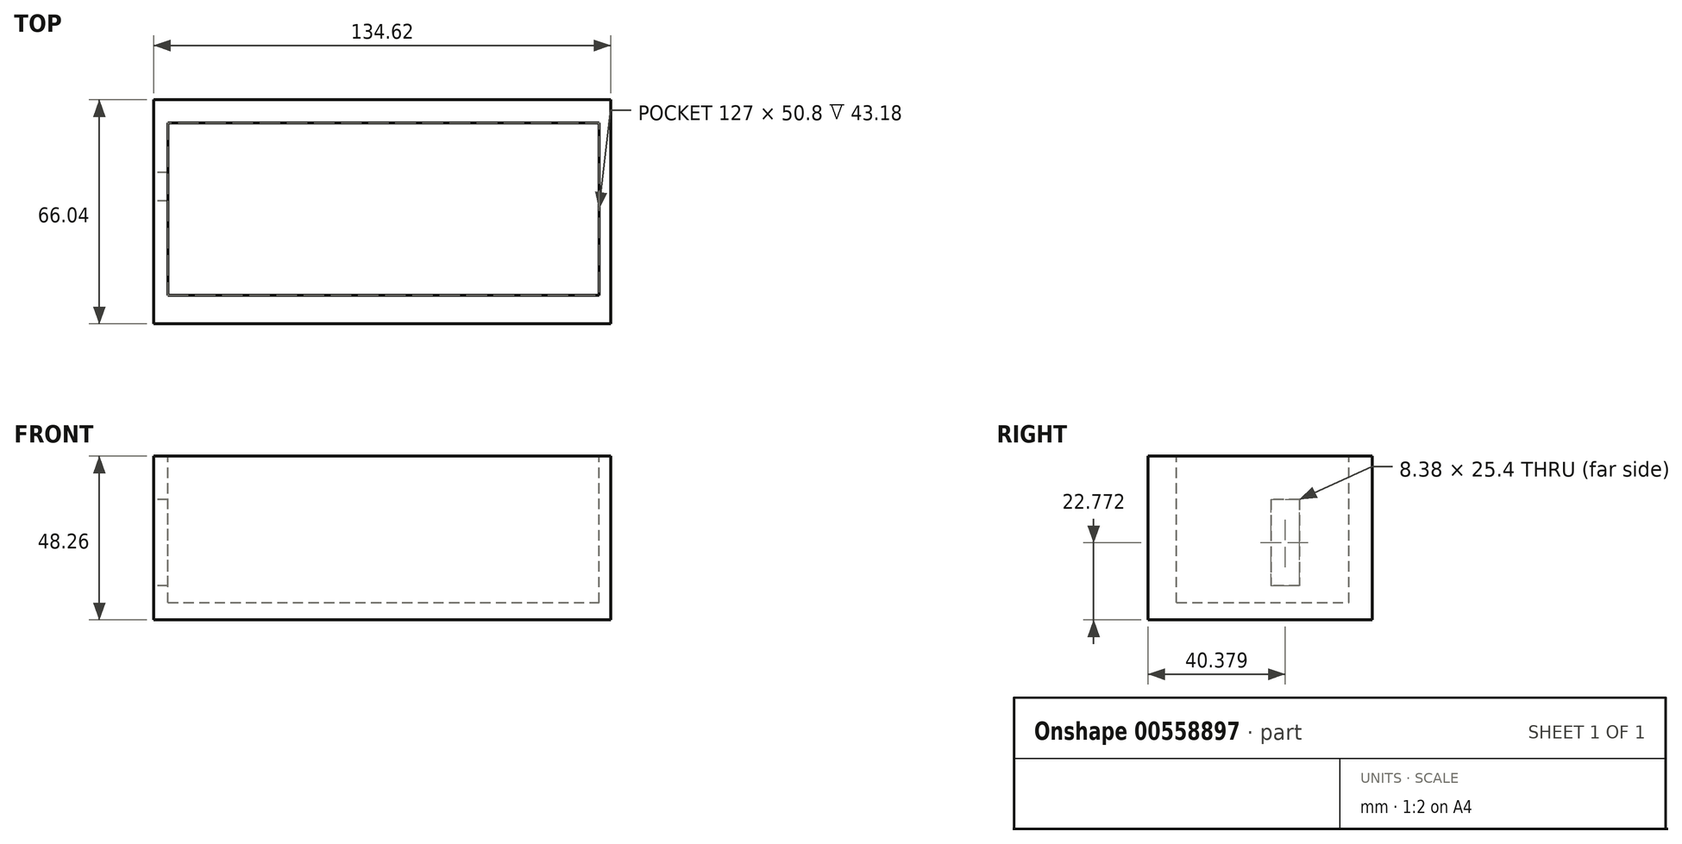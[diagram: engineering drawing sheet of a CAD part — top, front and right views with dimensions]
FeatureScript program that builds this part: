
annotation { "Feature Type Name" : "Feature", "Feature Type Description" : "" }
export const myFeature = defineFeature(function(context is Context, id is Id, definition is map)
    precondition{}
    {
        {
            var Q0;
            Q0=qCreatedBy(makeId("Top.planeOp"),FACE);
            var sketch = newSketch(context, id + "F0", { "sketchPlane" : qUnion([Q0])});
            skLineSegment(sketch, "E0.bottom", {"start": v(-63.14, -44.57) * mm, "end": v(71.48, -44.57) * mm});
            skLineSegment(sketch, "E0.top", {"start": v(-63.14, 21.47) * mm, "end": v(71.48, 21.47) * mm});
            skLineSegment(sketch, "E0.left", {"start": v(-63.14, -44.57) * mm, "end": v(-63.14, 21.47) * mm});
            skLineSegment(sketch, "E0.right", {"start": v(71.48, -44.57) * mm, "end": v(71.48, 21.47) * mm});
            skSolve(sketch);
        }
        {
            var Q0;
            Q0=makeQuery(id+"F0.imprint","IMPRINT",FACE,{"disambiguationData":[TD([[makeQuery(id+"F0.imprint","IMPRINT",EDGE,{"derivedFrom":sQuery(id+"F0.wireOp",EDGE,"E0.bottom")}),1.0]])]});
            extrude(context, id + "F1", {"entities" : qUnion([Q0]), "depth" : 48.26 * mm, "offsetDistance" : 25.4 * mm});
        }
        {
            var Q0;
            Q0=makeQuery(id+"F1.opExtrude","CAP_FACE",FACE,{"disambiguationData":[OSD([sQuery(id+"F0.wireOp",EDGE,"E0.bottom"),sQuery(id+"F0.wireOp",EDGE,"E0.top"),sQuery(id+"F0.wireOp",EDGE,"E0.left"),sQuery(id+"F0.wireOp",EDGE,"E0.right")])],"isStart":false});
            var sketch = newSketch(context, id + "F2", { "sketchPlane" : qUnion([Q0])});
            skLineSegment(sketch, "E1.bottom", {"start": v(-58.95, -36.15) * mm, "end": v(68.05, -36.15) * mm});
            skLineSegment(sketch, "E1.top", {"start": v(-58.95, 14.65) * mm, "end": v(68.05, 14.65) * mm});
            skLineSegment(sketch, "E1.left", {"start": v(-58.95, -36.15) * mm, "end": v(-58.95, 14.65) * mm});
            skLineSegment(sketch, "E1.right", {"start": v(68.05, -36.15) * mm, "end": v(68.05, 14.65) * mm});
            skSolve(sketch);
        }
        {
            var Q0;
            Q0=makeQuery(id+"F2.imprint","IMPRINT",FACE,{"disambiguationData":[TD([[makeQuery(id+"F2.imprint","IMPRINT",EDGE,{"derivedFrom":sQuery(id+"F2.wireOp",EDGE,"E1.bottom")}),1.0]])]});
            extrude(context, id + "F3", {"entities" : qUnion([Q0]), "operationType" : NewBodyOperationType.REMOVE, "oppositeDirection" : true, "depth" : 43.18 * mm, "offsetDistance" : 25.4 * mm});
        }
        {
            var Q0;
            Q0=makeQuery(id+"F1.opExtrude","SWEPT_FACE",FACE,{"disambiguationData":[OSD([sQuery(id+"F0.wireOp",EDGE,"E0.left")])]});
            var sketch = newSketch(context, id + "F4", { "sketchPlane" : qUnion([Q0])});
            skLineSegment(sketch, "E2.bottom", {"start": v(0, 35.47) * mm, "end": v(8.38, 35.47) * mm});
            skLineSegment(sketch, "E2.top", {"start": v(0, 10.07) * mm, "end": v(8.38, 10.07) * mm});
            skLineSegment(sketch, "E2.left", {"start": v(0, 35.47) * mm, "end": v(0, 10.07) * mm});
            skLineSegment(sketch, "E2.right", {"start": v(8.38, 35.47) * mm, "end": v(8.38, 10.07) * mm});
            skSolve(sketch);
        }
        {
            var Q0;
            Q0=makeQuery(id+"F4.imprint","IMPRINT",FACE,{"disambiguationData":[TD([[makeQuery(id+"F4.imprint","IMPRINT",EDGE,{"derivedFrom":sQuery(id+"F4.wireOp",EDGE,"E2.bottom")}),-1.0]])]});
            extrude(context, id + "F5", {"entities" : qUnion([Q0]), "operationType" : NewBodyOperationType.REMOVE, "oppositeDirection" : true, "depth" : 7.62 * mm, "offsetDistance" : 25.4 * mm});
        }
    });
